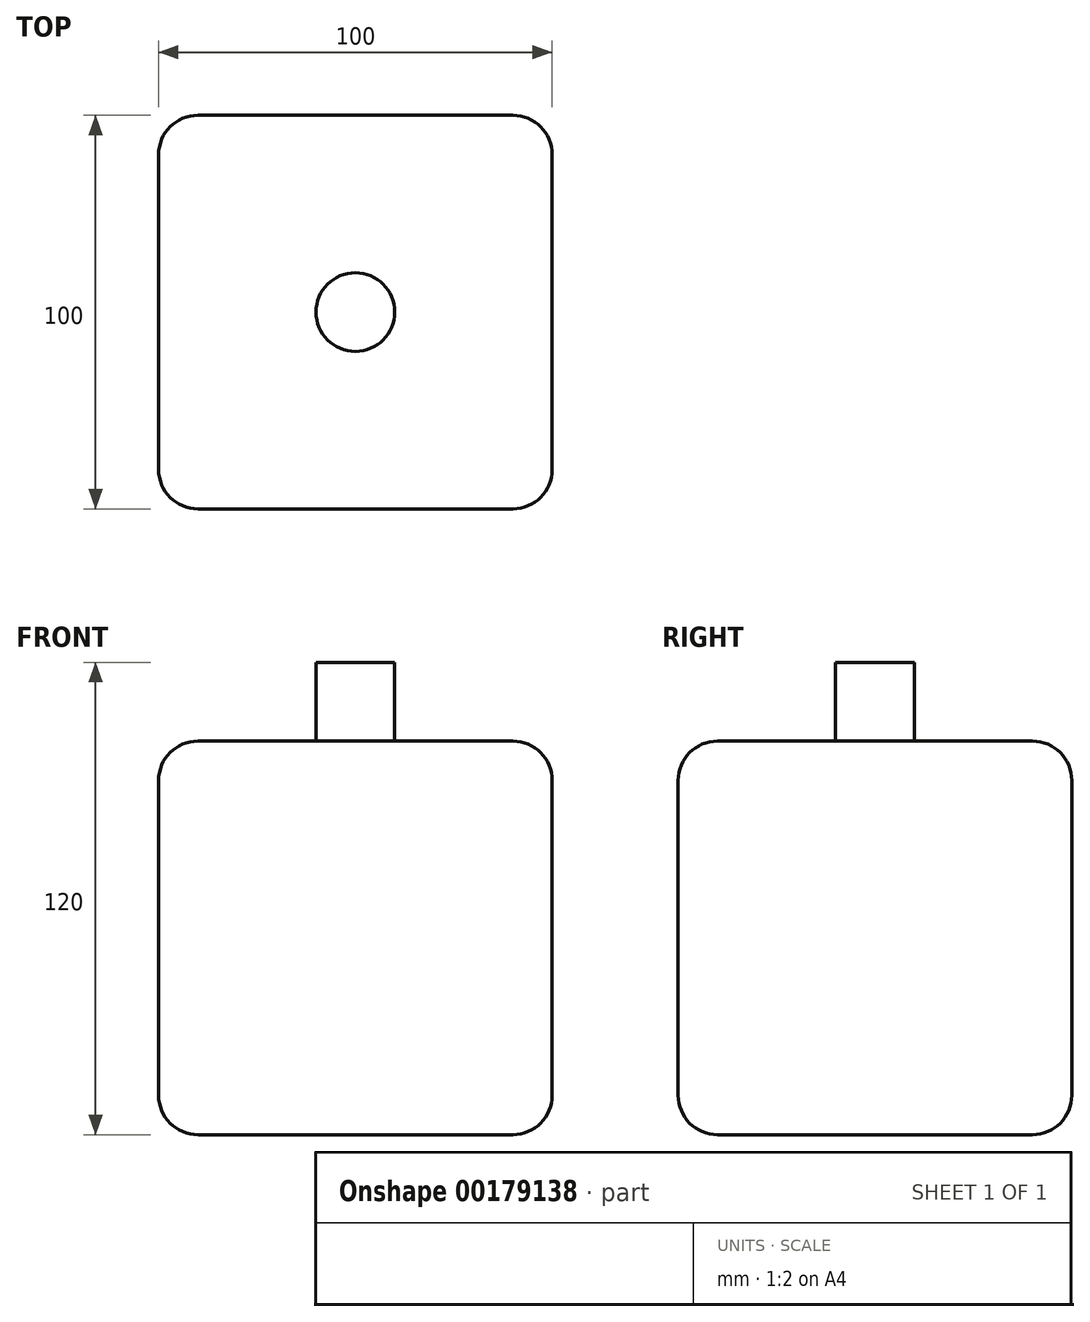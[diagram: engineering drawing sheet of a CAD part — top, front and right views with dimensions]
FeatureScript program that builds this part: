
annotation { "Feature Type Name" : "Feature", "Feature Type Description" : "" }
export const myFeature = defineFeature(function(context is Context, id is Id, definition is map)
    precondition{}
    {
        {
            var Q0;
            Q0=qCreatedBy(makeId("Top.planeOp"),FACE);
            var sketch = newSketch(context, id + "F0", { "sketchPlane" : qUnion([Q0])});
            skLineSegment(sketch, "E0", {"start": v(0, 0) * mm, "end": v(100, 0) * mm});
            skLineSegment(sketch, "E1", {"start": v(100, 0) * mm, "end": v(100, 100) * mm});
            skLineSegment(sketch, "E2", {"start": v(100, 100) * mm, "end": v(0, 100) * mm});
            skLineSegment(sketch, "E3", {"start": v(0, 100) * mm, "end": v(0, 0) * mm});
            skSolve(sketch);
        }
        {
            var Q0;
            Q0=makeQuery(id+"F0.imprint","IMPRINT",FACE,{"disambiguationData":[TD([[makeQuery(id+"F0.imprint","IMPRINT",EDGE,{"derivedFrom":sQuery(id+"F0.wireOp",EDGE,"E0")}),1.0]])]});
            extrude(context, id + "F1", {"entities" : qUnion([Q0]), "depth" : 100 * mm});
        }
        {
            var Q0;
            Q0=makeQuery(id+"F1.opExtrude","CAP_FACE",FACE,{"disambiguationData":[OSD([sQuery(id+"F0.wireOp",EDGE,"E0"),sQuery(id+"F0.wireOp",EDGE,"E1"),sQuery(id+"F0.wireOp",EDGE,"E2"),sQuery(id+"F0.wireOp",EDGE,"E3")])],"isStart":false});
            var sketch = newSketch(context, id + "F2", { "sketchPlane" : qUnion([Q0])});
            skLineSegment(sketch, "E4", {"start": v(0, 100) * mm, "end": v(100, 0) * mm, "construction": true});
            skLineSegment(sketch, "E5", {"start": v(100, 100) * mm, "end": v(0, 0) * mm, "construction": true});
            skCircle(sketch, "E6", {"center": v(50, 50) * mm, "radius": 10 * mm});
            skSolve(sketch);
        }
        {
            var Q0;
            Q0=makeQuery(id+"F2.imprint","IMPRINT",FACE,{"disambiguationData":[TD([[makeQuery(id+"F2.imprint","IMPRINT",EDGE,{"derivedFrom":sQuery(id+"F2.wireOp",EDGE,"E6")}),1.0]])]});
            extrude(context, id + "F3", {"entities" : qUnion([Q0]), "operationType" : NewBodyOperationType.ADD, "depth" : 20 * mm});
        }
        {
            var Q0;
            Q0=makeQuery(id+"F1.opExtrude","SWEPT_FACE",FACE,{"disambiguationData":[OSD([sQuery(id+"F0.wireOp",EDGE,"E0")])]});
            var Q1;
            Q1=makeQuery(id+"F1.opExtrude","SWEPT_FACE",FACE,{"disambiguationData":[OSD([sQuery(id+"F0.wireOp",EDGE,"E1")])]});
            var Q2;
            Q2=makeQuery(id+"F1.opExtrude","SWEPT_FACE",FACE,{"disambiguationData":[OSD([sQuery(id+"F0.wireOp",EDGE,"E2")])]});
            var Q3;
            Q3=makeQuery(id+"F1.opExtrude","SWEPT_FACE",FACE,{"disambiguationData":[OSD([sQuery(id+"F0.wireOp",EDGE,"E3")])]});
            fillet(context, id + "F4", {"entities" : qUnion([Q0, Q1, Q2, Q3]), "radius" : 10 * mm, "tangentPropagation" : true, "allowEdgeOverflow" : false});
        }
    });
